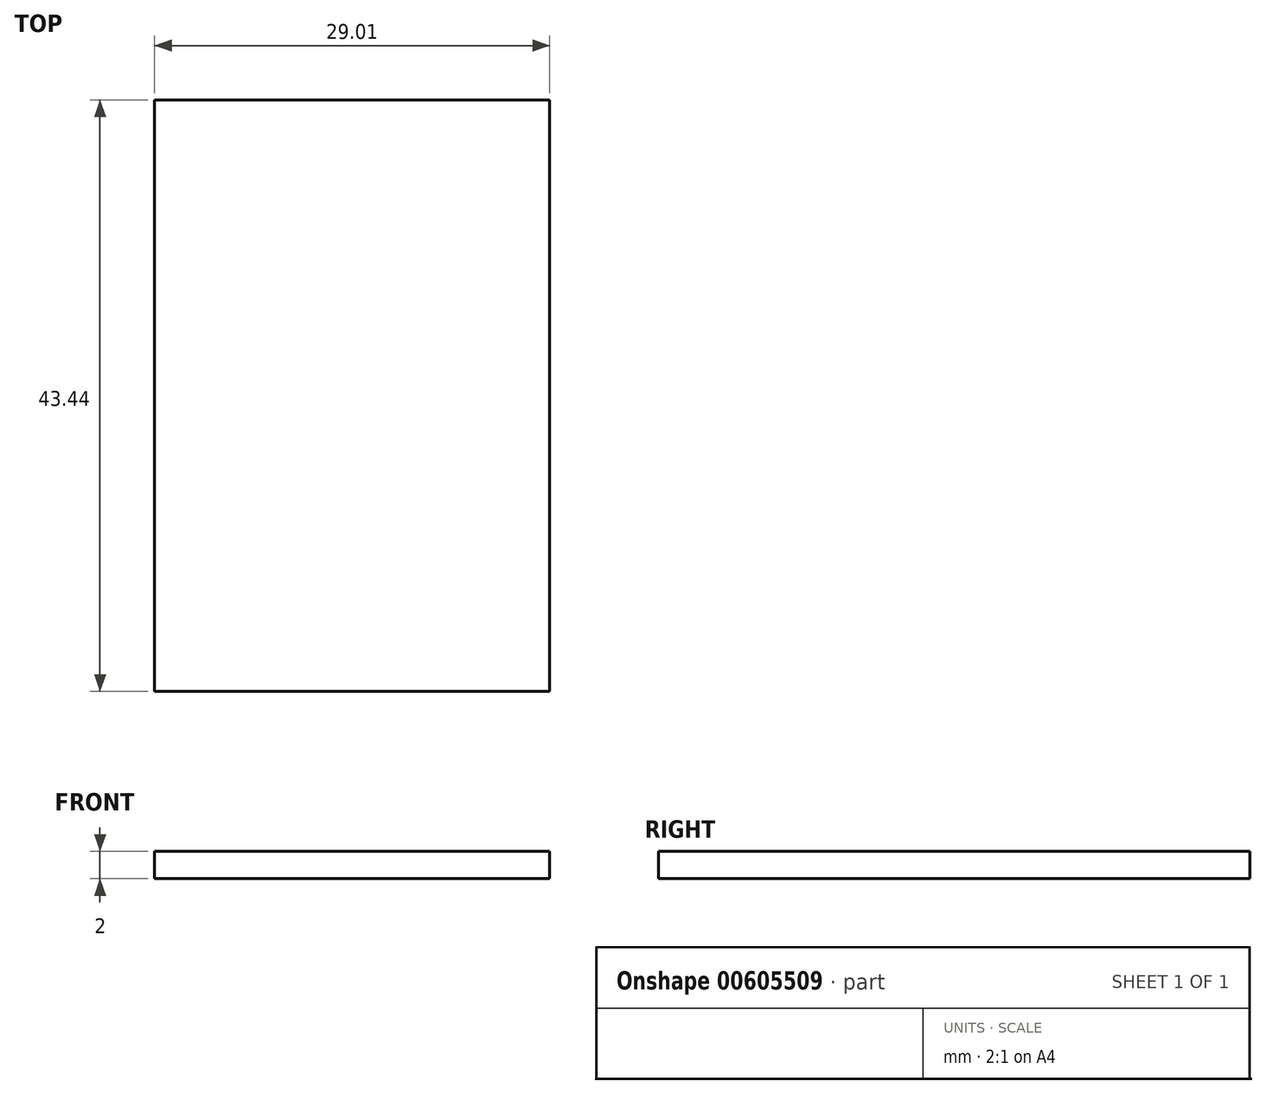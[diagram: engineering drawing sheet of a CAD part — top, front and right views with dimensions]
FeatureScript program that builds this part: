
annotation { "Feature Type Name" : "Feature", "Feature Type Description" : "" }
export const myFeature = defineFeature(function(context is Context, id is Id, definition is map)
    precondition{}
    {
        {
            var Q0;
            Q0=qCreatedBy(makeId("Top.planeOp"),FACE);
            var sketch = newSketch(context, id + "F0", { "sketchPlane" : qUnion([Q0])});
            skLineSegment(sketch, "E0", {"start": v(0, 0) * mm, "end": v(0, -43.44) * mm});
            skLineSegment(sketch, "E1", {"start": v(0, -43.44) * mm, "end": v(29, -43.44) * mm});
            skLineSegment(sketch, "E2", {"start": v(29, -43.44) * mm, "end": v(29, 0) * mm});
            skLineSegment(sketch, "E3", {"start": v(29, 0) * mm, "end": v(0, 0) * mm});
            skSolve(sketch);
        }
        {
            var Q0;
            Q0 = qSketchRegion(id + "F0", true);
            extrude(context, id + "F1", {"entities" : qUnion([Q0]), "depth" : 2 * mm, "offsetDistance" : 25.4 * mm});
        }
    });
